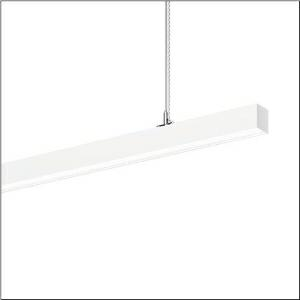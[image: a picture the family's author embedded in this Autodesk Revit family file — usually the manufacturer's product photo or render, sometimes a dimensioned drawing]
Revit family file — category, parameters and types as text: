
# Revit family: silica_r__21_51mx30tct9w_581c
name_source: partatom
category: Lighting Fixtures
units: mm (PartAtom-declared; Revit-internal decimal feet)

## family parameters
Cut with Voids When Loaded = No
Host = Face
Light Source = No
Part Type = Normal
Room Calculation Point = No
Round Connector Dimension = Use Diameter
Shared = No

## types (1)
- --- (1 x LED, 10300 lm, 84.4 W, 6500K)
    Apparent Load = 84 VA
    CIE Flux Codes = 47 79 96 58 100
    Color Rendering = 80
    Color Temperature = 6500K
    Default Elevation = 1800 mm
    Description = Silica® 21, office luminaire, primary optical cover: cover, of PMMA, opal, light emission: direct/indirect distribution, primary light characteristic: symmetric, installation type: suspended mounting, LED, rated luminous flux: 10.300lm, luminous efficacy: 116lm/W, light colour: 8tw, colour temperature: 2700..6500K, control gear: ECG DALI, with terminal, 3+2-pole, max. 2.5mm², mains connection: 220..240V, AC, 50/60Hz, rated input power: 88.7W, luminaire housing, of aluminium, traffic white (RAL 9016), length: 3.004mm, width: 53mm, height: 53mm, protection rating (complete): IP20, insulation class (complete): insulation class I (protective earthing), certification: CE, permissible operating ambient temperature: 0..+35°C, standard: EN 50419, packaging unit: 1 piece
    Height = 53 mm
    Lamp = 1 x LED
    Lamp Light Flux = 10300 lm
    Lamp Power = 84.4 W
    Lamp count = 1
    Length = 3004 mm
    Luminous efficacy = 122 lm/W
    Manufacturer = Siteco
    ModVariant = No
    Model = 51MX30TCT9W
    Mounting Place = Ceiling
    Mounting Type = Pendant
    Number of Poles = 1
    OnlyDefault = Yes
    Power Factor = 1
    Product Name = Silica® 21
    Product group = office luminaire | ceiling pendant
    ProductGroupID = 905
    Protection Class = Protection class I
    Protection Degree = IP 20
    RLX_Detail_Level = 1
    RlxData = <blob elided: 18041 chars, md5=86282982>
    Socket = socket
    Standby Power = 0 W
    System Light Flux = 10300 lm
    System Power = 84 W
    Type Comments = individual setting
    Type Image = l_1251642.jpg
    URL = http://relux.com
    VarID = @adj_045735
    Voltage = 0 V
    Weight = 0.00 kg
    Width = 53 mm

## geometry (parser evidence)
native form markers: Blend x4, Sweep x16
no freeform markers — native parametric forms only
